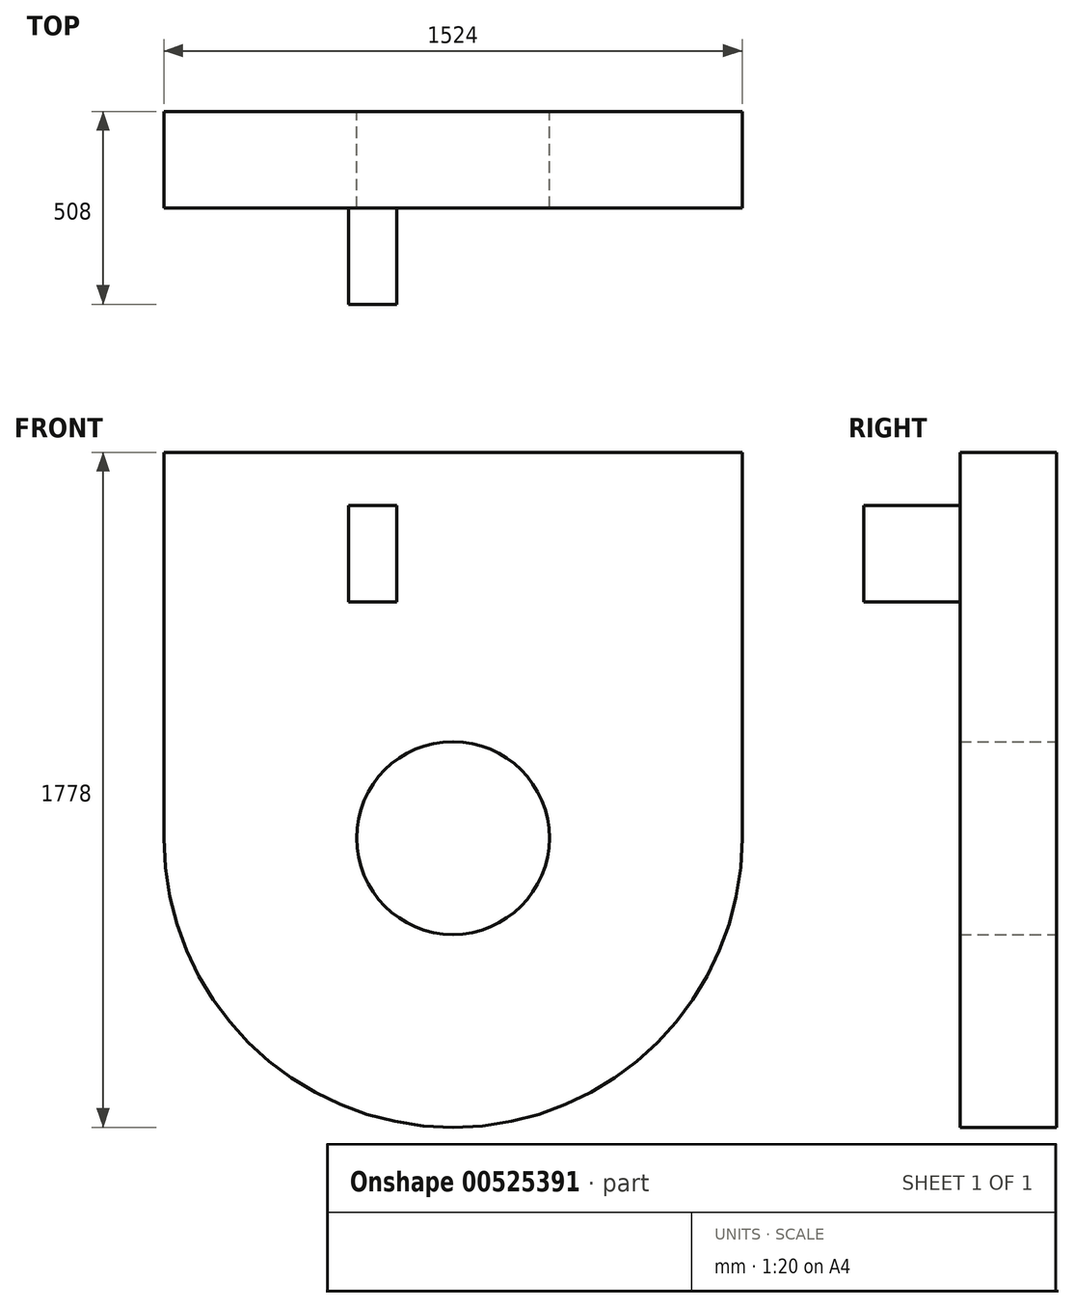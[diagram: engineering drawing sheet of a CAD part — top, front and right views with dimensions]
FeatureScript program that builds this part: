
annotation { "Feature Type Name" : "Feature", "Feature Type Description" : "" }
export const myFeature = defineFeature(function(context is Context, id is Id, definition is map)
    precondition{}
    {
        {
            var Q0;
            Q0=qCreatedBy(makeId("Front.planeOp"),FACE);
            var sketch = newSketch(context, id + "F0", { "sketchPlane" : qUnion([Q0])});
            skLineSegment(sketch, "E0.bottom", {"start": v(-1524, 1016) * mm, "end": v(0, 1016) * mm});
            skLineSegment(sketch, "E0.left", {"start": v(-1524, 1016) * mm, "end": v(-1524, 0) * mm});
            skLineSegment(sketch, "E0.right", {"start": v(0, 1016) * mm, "end": v(0, 0) * mm});
            skLineSegment(sketch, "E1", {"start": v(-1524, 254) * mm, "end": v(0, 254) * mm});
            skLineSegment(sketch, "E2", {"start": v(-254, 1016) * mm, "end": v(-254, 762) * mm});
            skLineSegment(sketch, "E3", {"start": v(-254, 762) * mm, "end": v(0, 762) * mm});
            skCircle(sketch, "E4", {"center": v(-762, 0) * mm, "radius": 254 * mm});
            skArc(sketch, "E5", {"start": v(-1524, 0) * mm, "mid": v(-762, -762) * mm, "end": v(0, 0) * mm});
            skSolve(sketch);
        }
        {
            var Q0;
            Q0 = qSketchRegion(id + "F0", true);
            extrude(context, id + "F1", {"entities" : qUnion([Q0]), "depth" : 254 * mm, "offsetDistance" : 25.4 * mm});
        }
        {
            var Q0;
            Q0=makeQuery(id+"F1.opExtrude","CAP_FACE",FACE,{"disambiguationData":[OSD([sQuery(id+"F0.wireOp",EDGE,"E0.bottom"),sQuery(id+"F0.wireOp",EDGE,"E0.left"),sQuery(id+"F0.wireOp",EDGE,"E0.right"),sQuery(id+"F0.wireOp",EDGE,"E4"),sQuery(id+"F0.wireOp",EDGE,"E5")])],"isStart":false});
            var sketch = newSketch(context, id + "F2", { "sketchPlane" : qUnion([Q0])});
            skLineSegment(sketch, "E6", {"start": v(-1037.24, 875.67) * mm, "end": v(-910.24, 875.67) * mm});
            skLineSegment(sketch, "E7", {"start": v(-910.24, 875.67) * mm, "end": v(-910.24, 621.67) * mm});
            skLineSegment(sketch, "E8", {"start": v(-910.24, 621.67) * mm, "end": v(-1037.24, 621.67) * mm});
            skLineSegment(sketch, "E9", {"start": v(-1037.24, 621.67) * mm, "end": v(-1037.24, 875.67) * mm});
            skSolve(sketch);
        }
        {
            var Q0;
            Q0=makeQuery(id+"F2.imprint","IMPRINT",FACE,{"disambiguationData":[TD([[makeQuery(id+"F2.imprint","IMPRINT",EDGE,{"derivedFrom":sQuery(id+"F2.wireOp",EDGE,"E6")}),-1.0]])]});
            extrude(context, id + "F3", {"entities" : qUnion([Q0]), "operationType" : NewBodyOperationType.ADD, "depth" : 127 * mm, "offsetDistance" : 25.4 * mm});
        }
        {
            var Q0;
            Q0=makeQuery(id+"F3.opExtrude","CAP_FACE",FACE,{"disambiguationData":[OSD([sQuery(id+"F2.wireOp",EDGE,"E6"),sQuery(id+"F2.wireOp",EDGE,"E7"),sQuery(id+"F2.wireOp",EDGE,"E8"),sQuery(id+"F2.wireOp",EDGE,"E9")])],"isStart":false});
            extrude(context, id + "F4", {"entities" : qUnion([Q0]), "operationType" : NewBodyOperationType.ADD, "depth" : 127 * mm, "offsetDistance" : 25.4 * mm});
        }
    });
